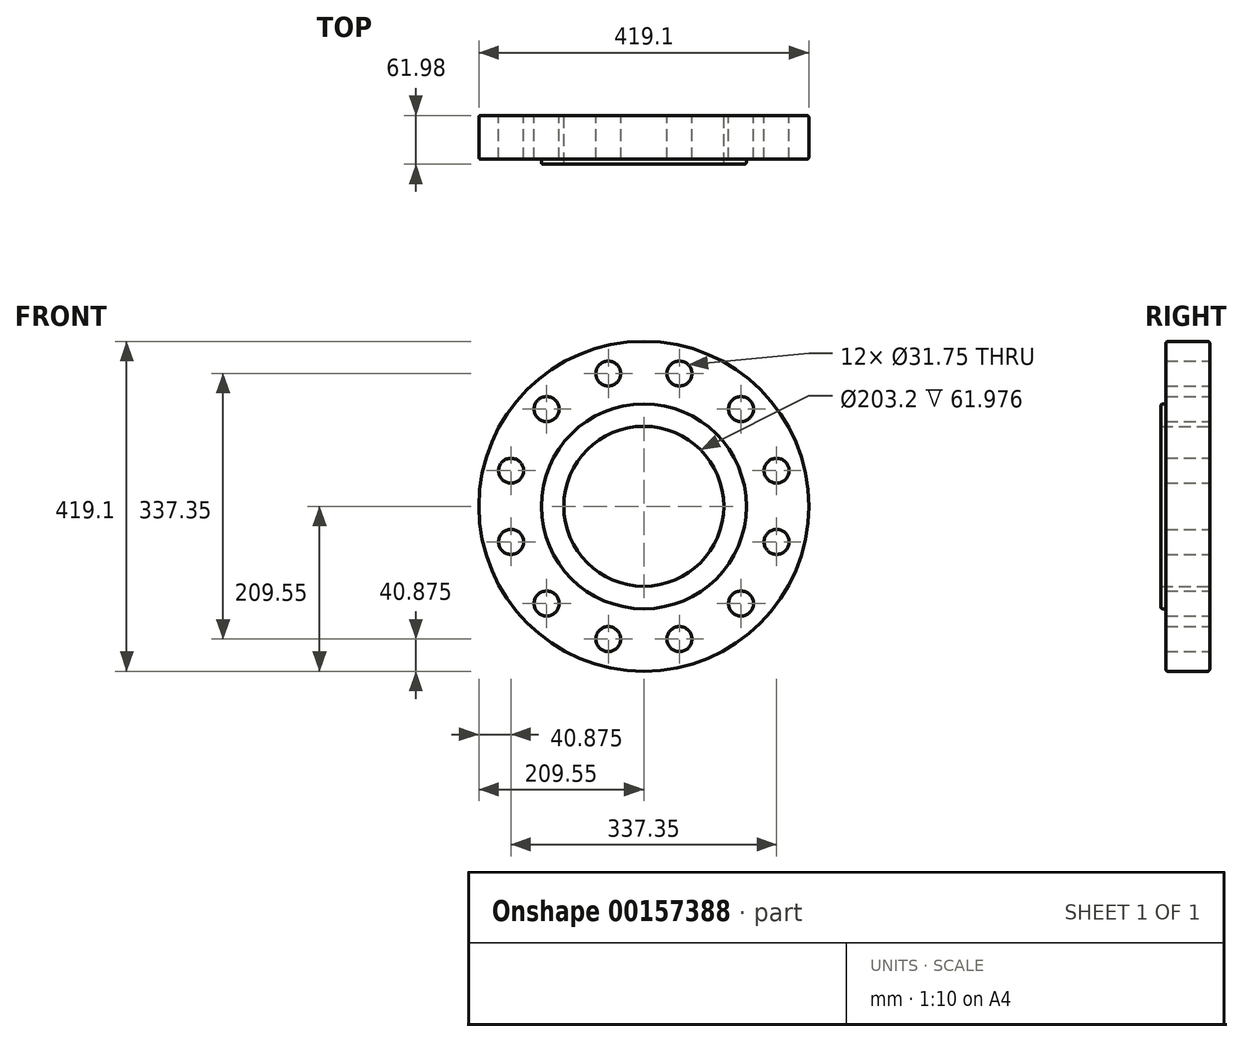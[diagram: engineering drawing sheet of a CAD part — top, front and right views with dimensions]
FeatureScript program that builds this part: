
annotation { "Feature Type Name" : "Feature", "Feature Type Description" : "" }
export const myFeature = defineFeature(function(context is Context, id is Id, definition is map)
    precondition{}
    {
        {
            var Q0;
            Q0=qCreatedBy(makeId("Front.planeOp"),FACE);
            var sketch = newSketch(context, id + "F0", { "sketchPlane" : qUnion([Q0])});
            skCircle(sketch, "E0", {"center": v(0, 0) * mm, "radius": 209.55 * mm});
            skCircle(sketch, "E1", {"center": v(0, 0) * mm, "radius": 101.6 * mm});
            skCircle(sketch, "E2", {"center": v(45.2, 168.67) * mm, "radius": 15.88 * mm});
            skCircle(sketch, "E3.1.0", {"center": v(-45.2, 168.67) * mm, "radius": 15.88 * mm});
            skCircle(sketch, "E3.2.0", {"center": v(-123.48, 123.48) * mm, "radius": 15.88 * mm});
            skCircle(sketch, "E3.3.0", {"center": v(-168.67, 45.2) * mm, "radius": 15.88 * mm});
            skCircle(sketch, "E3.4.0", {"center": v(-168.67, -45.2) * mm, "radius": 15.88 * mm});
            skCircle(sketch, "E3.5.0", {"center": v(-123.48, -123.48) * mm, "radius": 15.88 * mm});
            skCircle(sketch, "E3.6.0", {"center": v(-45.2, -168.67) * mm, "radius": 15.88 * mm});
            skCircle(sketch, "E3.7.0", {"center": v(45.2, -168.67) * mm, "radius": 15.88 * mm});
            skCircle(sketch, "E3.8.0", {"center": v(123.48, -123.48) * mm, "radius": 15.88 * mm});
            skCircle(sketch, "E3.9.0", {"center": v(168.67, -45.2) * mm, "radius": 15.88 * mm});
            skCircle(sketch, "E3.10.0", {"center": v(168.67, 45.2) * mm, "radius": 15.88 * mm});
            skCircle(sketch, "E3.11.0", {"center": v(123.48, 123.48) * mm, "radius": 15.88 * mm});
            skSolve(sketch);
        }
        {
            var Q0;
            Q0 = qSketchRegion(id + "F0", true);
            extrude(context, id + "F1", {"entities" : qUnion([Q0]), "depth" : 55.63 * mm});
        }
        {
            var Q0;
            Q0=makeQuery(id+"F1.opExtrude","CAP_FACE",FACE,{"disambiguationData":[OSD([sQuery(id+"F0.wireOp",EDGE,"E0"),sQuery(id+"F0.wireOp",EDGE,"E1"),sQuery(id+"F0.wireOp",EDGE,"E2"),sQuery(id+"F0.wireOp",EDGE,"E3.1.0"),sQuery(id+"F0.wireOp",EDGE,"E3.2.0"),sQuery(id+"F0.wireOp",EDGE,"E3.3.0"),sQuery(id+"F0.wireOp",EDGE,"E3.4.0"),sQuery(id+"F0.wireOp",EDGE,"E3.5.0"),sQuery(id+"F0.wireOp",EDGE,"E3.6.0"),sQuery(id+"F0.wireOp",EDGE,"E3.7.0"),sQuery(id+"F0.wireOp",EDGE,"E3.8.0"),sQuery(id+"F0.wireOp",EDGE,"E3.9.0"),sQuery(id+"F0.wireOp",EDGE,"E3.10.0"),sQuery(id+"F0.wireOp",EDGE,"E3.11.0")])],"isStart":false});
            var sketch = newSketch(context, id + "F2", { "sketchPlane" : qUnion([Q0])});
            skCircle(sketch, "E4", {"center": v(0, 0) * mm, "radius": 130.18 * mm});
            skCircle(sketch, "E5", {"center": v(0, 0) * mm, "radius": 101.6 * mm});
            skSolve(sketch);
        }
        {
            var Q0;
            Q0 = qSketchRegion(id + "F2", true);
            extrude(context, id + "F3", {"entities" : qUnion([Q0]), "operationType" : NewBodyOperationType.ADD, "depth" : 6.35 * mm});
        }
        {
            var Q0;
            Q0=makeQuery(id+"F1.opExtrude","CAP_EDGE",EDGE,{"disambiguationData":[OSD([sQuery(id+"F0.wireOp",EDGE,"E0")])],"isStart":false});
            var Q1;
            Q1=makeQuery(id+"F1.opExtrude","CAP_EDGE",EDGE,{"disambiguationData":[OSD([sQuery(id+"F0.wireOp",EDGE,"E0")])],"isStart":true});
            var Q2;
            Q2=makeQuery(id+"F3.opExtrude","CAP_EDGE",EDGE,{"disambiguationData":[OSD([sQuery(id+"F2.wireOp",EDGE,"E4")])],"isStart":false});
            var Q3;
            Q3=makeQuery(id+"F3.opExtrude","CAP_EDGE",EDGE,{"disambiguationData":[OSD([sQuery(id+"F2.wireOp",EDGE,"E4")])],"isStart":true});
            fillet(context, id + "F4", {"entities" : qUnion([Q0, Q1, Q2, Q3]), "radius" : 2.54 * mm, "tangentPropagation" : true, "allowEdgeOverflow" : false});
        }
    });
